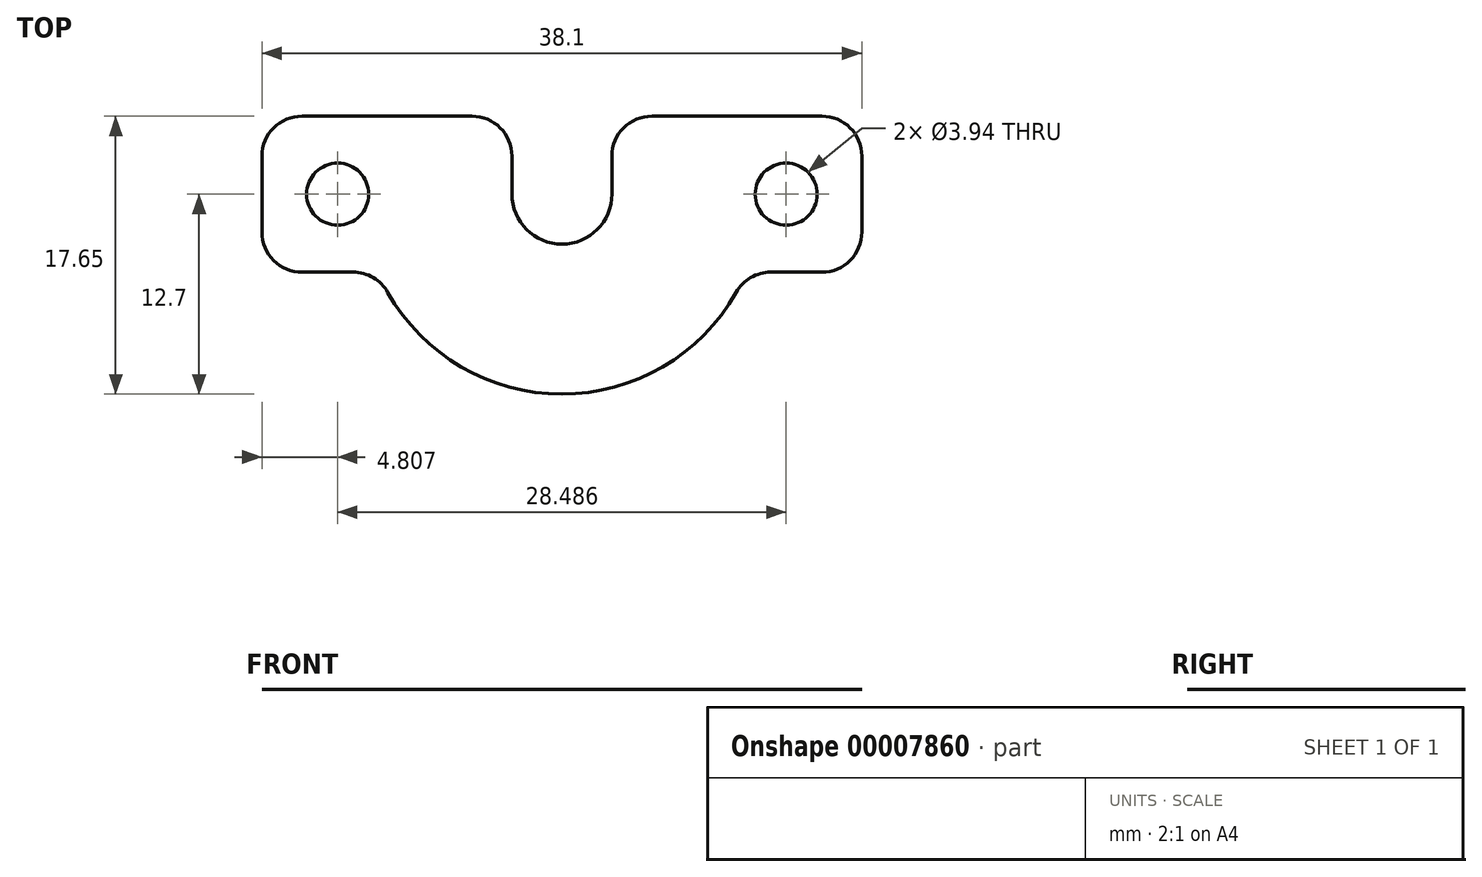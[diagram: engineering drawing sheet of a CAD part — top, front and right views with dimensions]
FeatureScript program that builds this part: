
annotation { "Feature Type Name" : "Feature", "Feature Type Description" : "" }
export const myFeature = defineFeature(function(context is Context, id is Id, definition is map)
    precondition{}
    {
        {
            var Q0;
            Q0=qCreatedBy(makeId("Top.planeOp"),FACE);
            var sketch = newSketch(context, id + "F0", { "sketchPlane" : qUnion([Q0])});
            skArc(sketch, "E0", {"start": v(-3.18, 0) * mm, "mid": v(0, -3.18) * mm, "end": v(3.18, 0) * mm});
            skCircle(sketch, "E1", {"center": v(14.24, 0) * mm, "radius": 1.97 * mm});
            skCircle(sketch, "E2", {"center": v(-14.24, 0) * mm, "radius": 1.97 * mm});
            skPoint(sketch, "E3", {"position": v(12.57, 0) * mm});
            skPoint(sketch, "E4", {"position": v(15.91, 0) * mm});
            skLineSegment(sketch, "E5", {"start": v(12.57, 0) * mm, "end": v(15.91, 0) * mm, "construction": true});
            skLineSegment(sketch, "E6", {"start": v(-15.91, 0) * mm, "end": v(-12.57, 0) * mm, "construction": true});
            skLineSegment(sketch, "E7", {"start": v(-12.57, 0) * mm, "end": v(12.57, 0) * mm, "construction": true});
            skLineSegment(sketch, "E8", {"start": v(-3.18, 0) * mm, "end": v(-3.18, 4.95) * mm});
            skLineSegment(sketch, "E9", {"start": v(-3.18, 4.95) * mm, "end": v(-19.05, 4.95) * mm});
            skLineSegment(sketch, "E10", {"start": v(-19.05, 4.95) * mm, "end": v(-19.05, -4.95) * mm});
            skLineSegment(sketch, "E11", {"start": v(-19.05, -4.95) * mm, "end": v(19.05, -4.95) * mm});
            skLineSegment(sketch, "E12", {"start": v(19.05, -4.95) * mm, "end": v(19.05, 4.95) * mm});
            skLineSegment(sketch, "E13", {"start": v(19.05, 4.95) * mm, "end": v(3.18, 4.95) * mm});
            skLineSegment(sketch, "E14", {"start": v(3.18, 4.95) * mm, "end": v(3.18, 0) * mm});
            skLineSegment(sketch, "E15", {"start": v(-15.91, 0) * mm, "end": v(-19.05, 0) * mm, "construction": true});
            skLineSegment(sketch, "E16", {"start": v(0, 0) * mm, "end": v(0, -4.95) * mm, "construction": true});
            skArc(sketch, "E17", {"start": v(-11.7, -4.95) * mm, "mid": v(0, -12.7) * mm, "end": v(11.7, -4.95) * mm});
            skSolve(sketch);
        }
        {
            var Q0;
            Q0=makeQuery(id+"F0.imprint","IMPRINT",FACE,{"disambiguationData":[TD([[makeQuery(id+"F0.imprint","IMPRINT",EDGE,{"derivedFrom":sQuery(id+"F0.wireOp",EDGE,"E0")}),-1.0]])]});
            var Q1;
            {var subQ1=sQuery(id+"F0.wireOp",EDGE,"236b215a-24b7-4c7b-b2cc-3c4630945286");Q1=makeQuery(id+"F0.imprint","IMPRINT",FACE,{"disambiguationData":[TD([[makeQuery(id+"F0.imprint","IMPRINT",EDGE,{"derivedFrom":subQ1}),1.0]])]});}
            var Q2;
            {var subQ1=sQuery(id+"F0.wireOp",EDGE,"1f6d2c22-eec1-4b19-a858-0aa824ffc2f2");Q2=makeQuery(id+"F0.imprint","IMPRINT",FACE,{"disambiguationData":[TD([[makeQuery(id+"F0.imprint","IMPRINT",EDGE,{"derivedFrom":subQ1}),-1.0]])]});}
            var Q3;
            {var subQ0=sQuery(id+"F0.wireOp",EDGE,"E17");Q3=makeQuery(id+"F0.imprint","IMPRINT",FACE,{"disambiguationData":[TD([[makeQuery(id+"F0.imprint","IMPRINT",EDGE,{"derivedFrom":subQ0}),1.0]])]});}
            extrude(context, id + "F1", {"entities" : qUnion([Q0, Q1, Q2, Q3]), "depth" : 1 / 406.4 * mm});
        }
        {
            var Q0;
            {var subQ0=sQuery(id+"F0.wireOp",EDGE,"E11");var subQ1=sQuery(id+"F0.wireOp",EDGE,"E17");Q0=makeQuery(id+"F1.opExtrude","SWEPT_EDGE",EDGE,{"disambiguationData":[OSD([subQ0,subQ1]),TDD([makeQuery(id+"F0.imprint","INTERSECT",VERTEX,{"disambiguationData":[OD(0.0)],"derivedFrom":[subQ0,subQ1]})])]});}
            var Q1;
            {var subQ0=sQuery(id+"F0.wireOp",EDGE,"E11");var subQ1=sQuery(id+"F0.wireOp",EDGE,"E17");Q1=makeQuery(id+"F1.opExtrude","SWEPT_EDGE",EDGE,{"disambiguationData":[OSD([subQ0,subQ1]),TDD([makeQuery(id+"F0.imprint","INTERSECT",VERTEX,{"disambiguationData":[OD(1.0)],"derivedFrom":[subQ0,subQ1]})])]});}
            var Q2;
            Q2=makeQuery(id+"F1.opExtrude","SWEPT_EDGE",EDGE,{"disambiguationData":[OSD([sQuery(id+"F0.wireOp",EDGE,"E11"),sQuery(id+"F0.wireOp",EDGE,"E12")])]});
            var Q3;
            Q3=makeQuery(id+"F1.opExtrude","SWEPT_EDGE",EDGE,{"disambiguationData":[OSD([sQuery(id+"F0.wireOp",EDGE,"E10"),sQuery(id+"F0.wireOp",EDGE,"E11")])]});
            var Q4;
            Q4=makeQuery(id+"F1.opExtrude","SWEPT_EDGE",EDGE,{"disambiguationData":[OSD([sQuery(id+"F0.wireOp",EDGE,"E12"),sQuery(id+"F0.wireOp",EDGE,"E13")])]});
            var Q5;
            Q5=makeQuery(id+"F1.opExtrude","SWEPT_EDGE",EDGE,{"disambiguationData":[OSD([sQuery(id+"F0.wireOp",EDGE,"E13"),sQuery(id+"F0.wireOp",EDGE,"E14")])]});
            var Q6;
            Q6=makeQuery(id+"F1.opExtrude","SWEPT_EDGE",EDGE,{"disambiguationData":[OSD([sQuery(id+"F0.wireOp",EDGE,"E8"),sQuery(id+"F0.wireOp",EDGE,"E9")])]});
            var Q7;
            Q7=makeQuery(id+"F1.opExtrude","SWEPT_EDGE",EDGE,{"disambiguationData":[OSD([sQuery(id+"F0.wireOp",EDGE,"E9"),sQuery(id+"F0.wireOp",EDGE,"E10")])]});
            fillet(context, id + "F2", {"entities" : qUnion([Q0, Q1, Q2, Q3, Q4, Q5, Q6, Q7]), "radius" : 2.54 * mm, "tangentPropagation" : true, "allowEdgeOverflow" : false});
        }
    });
